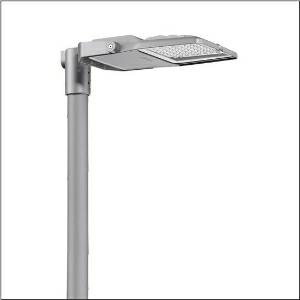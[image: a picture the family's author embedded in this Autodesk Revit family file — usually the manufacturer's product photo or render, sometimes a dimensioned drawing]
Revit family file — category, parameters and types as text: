
# Revit family: floodlight_fl_21_iq_mini___pl64_5xa7771b2e3a_ab64
name_source: partatom
category: Lighting Fixtures
units: mm (PartAtom-declared; Revit-internal decimal feet)

## family parameters
Cut with Voids When Loaded = No
Host = Face
Light Source = No
Part Type = Normal
Room Calculation Point = No
Round Connector Dimension = Use Diameter
Shared = No

## types (1)
- --- (1 x LED, 6020 lm, 45.5 W, 3000K)
    Apparent Load = 46 VA
    CIE Flux Codes = 28 80 98 100 100
    Color Rendering = 70
    Color Temperature = 3000K
    Default Elevation = 1800 mm
    Description = Floodlight FL 21 iQ mini, floodlight, primary light control with lens, of PMMA, primary optical cover: protective disc, of toughened safety glass, transparent, light distribution: PL64, light emission: direct distribution, installation type: surface-mounted, lamps: LED, High Power LED, rated values: 6.020lm | 45,5W | 132,3lm/W (begin service life); end service life: 6.020lm | 48W; at 50% lumin. flux: 3.010lm | 21,5W | 140lm/W, colour temperature: 3000K, colour rendering: CRI > 70, light colour: 730, light setting 1 begin service life: 100% | 6.020lm | 45,5W | 132,3lm/W | 3.000K, light setting 1 end service life: 48W, further light settings possible, control: Auto-Match, Temp-Guard, Lumen-Switch, Night-Set, Smart-Wire, Light-Fading, Desk-Remote (wireless, voltage-free reading and setting of iQ features in the workshop via application-optimized NFC function/RFID function), optimised constant luminous flux control (CLO 2.0), pre-setting: linear dimming characteristic, with terminal, 6-pole, mains connection: 220..240V, AC, 50/60Hz, luminaire housing, of diecast aluminium, powder-coated, SITECO metallic grey (DB 702S), corrosivity category C5 mid according to DIN EN ISO 12944suitable for swimming poolschlorine-resistant, sealing non-destructively replaceable, please order mast flange separately, mast bracket, of steel, galvanised, powder-coated, SITECO metallic grey (DB 702S), protection rating (complete): IP66, insulation class (complete): insulation class II (safety insulation), certification: CE, ENEC, VDE, protection symbol: D, impact resistance: IK08, permissible operating ambient temperature: -40..+40°C, permissible operating ambient temperature for outdoor applications: -40..+50°C, standard: DIN EN 12944, LABS conformity tested according to VDMA 24364:2018-05, packaging unit: 1 piece

Light Distribution: PL64
    Height = 70 mm
    Lamp = 1 x LED
    Lamp Light Flux = 6020 lm
    Lamp Power = 45.5 W
    Lamp count = 1
    Length = 485 mm
    Luminous efficacy = 132 lm/W
    Manufacturer = Siteco
    ModVariant = No
    Model = 5XA7771B2E3A
    Number of Poles = 1
    OnlyDefault = Yes
    Power Factor = 1
    Product Name = Floodlight FL 21 iQ mini | PL64
    Product group = floodlight | pylon annexe
    ProductGroupID = 6201
    Protection Class = Protection class II
    Protection Degree = IP 66
    RLX_Detail_Level = 1
    RLX_Emergency_Light_Flux = 0 lm
    RLX_Emergency_Type = 0
    RLX_Emergency_Type_DB = No
    RlxData = <blob elided: 101389 chars, md5=16a48620>
    Socket = socket
    Standby Power = 0 W
    System Light Flux = 6020 lm
    System Power = 46 W
    Type Comments = factory setting: luminous flux: 100 % | dim-lin: 254 | 463 mA
    Type Image = l_1007125.jpg
    URL = http://relux.com
    VarID = @adj_166631
    Voltage = 0 V
    Weight = 0.00 kg
    Width = 337 mm

## geometry (parser evidence)
native form markers: Blend x4, Sweep x12
no freeform markers — native parametric forms only
